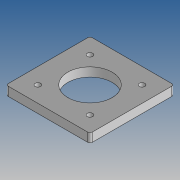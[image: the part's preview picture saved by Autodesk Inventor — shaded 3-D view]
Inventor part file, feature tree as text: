
AUTODESK INVENTOR PART (.ipt)
format: ipt  version: 2017 (Build 210142000, 142)  size: 104,448 bytes
history: native  units: mm
features: extrude x1, sketch x1
ambient origin geometry x8: Origin, YZ Plane, XZ Plane, XY Plane, X Axis, Y Axis, Z Axis, Center Point
bodies: Body1 (feature_tree)
feature tree (2):
  extrude  "Extrusión1"  Depth=2.0mm
  sketch  "Boceto1"  dims[d0=76.0mm d1=2.0mm d2=5.0mm d3=61.609459mm d4=40.0mm d5=8.0mm d6=0.0mm d23=47.1mm]
